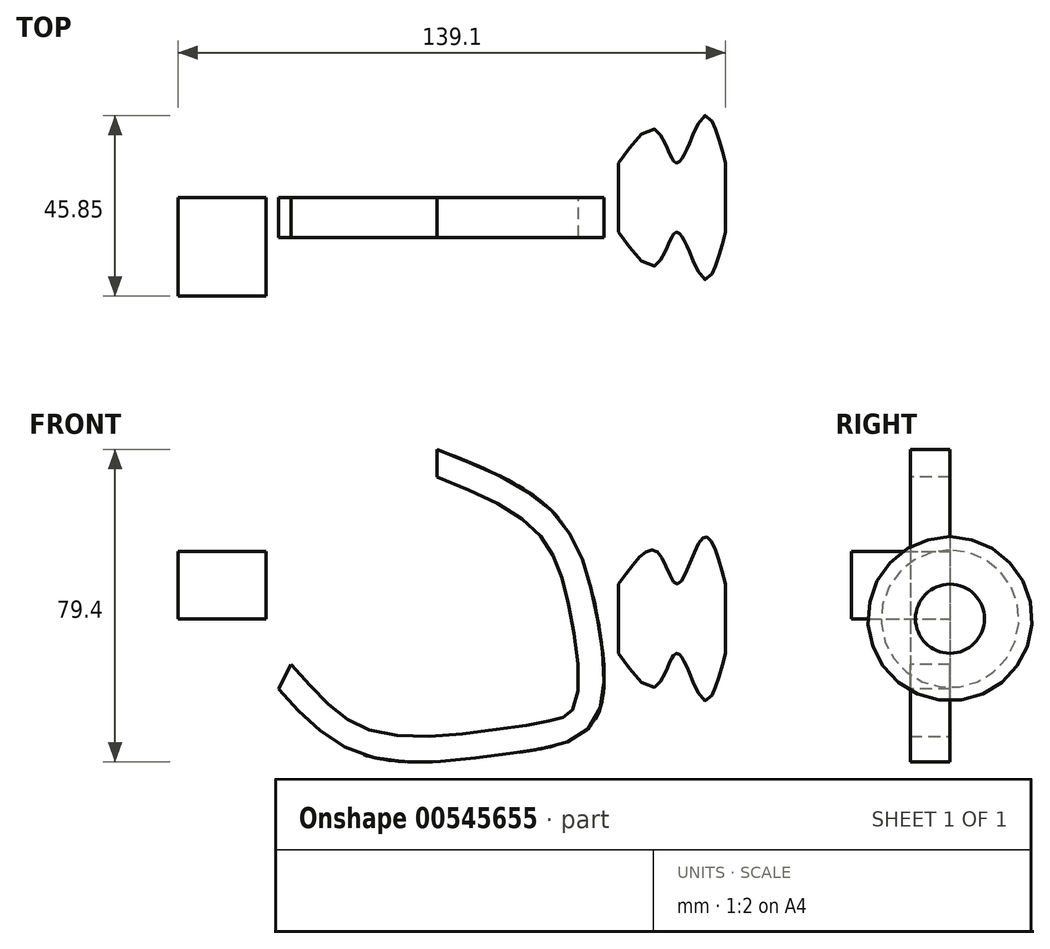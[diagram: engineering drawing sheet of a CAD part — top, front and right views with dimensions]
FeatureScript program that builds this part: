
annotation { "Feature Type Name" : "Feature", "Feature Type Description" : "" }
export const myFeature = defineFeature(function(context is Context, id is Id, definition is map)
    precondition{}
    {
        {
            var Q0;
            Q0=qCreatedBy(makeId("Front.planeOp"),FACE);
            var sketch = newSketch(context, id + "F0", { "sketchPlane" : qUnion([Q0])});
            skFitSpline(sketch, "E0", {"points": [v(0, 42.12) * mm, v(29.4, 25.89) * mm, v(39.93, 0) * mm, v(39.05, -25.89) * mm, v(18.87, -33.35) * mm, v(-18.43, -33.79) * mm, v(-39.93, -17.11) * mm], "startDerivative": vector(187.87, -73.92) * mm, "endDerivative": vector(-114.57, 127.43) * mm});
            skSolve(sketch);
        }
        {
            var Q0;
            Q0=qCreatedBy(makeId("Right.planeOp"),FACE);
            var sketch = newSketch(context, id + "F1", { "sketchPlane" : qUnion([Q0])});
            skLineSegment(sketch, "E1.bottom", {"start": v(0, 43) * mm, "end": v(-10.1, 43) * mm});
            skLineSegment(sketch, "E1.top", {"start": v(0, 35.98) * mm, "end": v(-10.1, 35.98) * mm});
            skLineSegment(sketch, "E1.left", {"start": v(0, 43) * mm, "end": v(0, 35.98) * mm});
            skLineSegment(sketch, "E1.right", {"start": v(-10.1, 43) * mm, "end": v(-10.1, 35.98) * mm});
            skSolve(sketch);
        }
        {
            var Q0;
            Q0=makeQuery(id+"F1.imprint","IMPRINT",FACE,{"disambiguationData":[TD([[makeQuery(id+"F1.imprint","IMPRINT",EDGE,{"derivedFrom":sQuery(id+"F1.wireOp",EDGE,"E1.bottom")}),1.0]])]});
            var Q1;
            Q1=sQuery(id+"F0.wireOp",EDGE,"E0");
            sweep(context, id + "F2", {"profiles" : qUnion([Q0]), "path" : qUnion([Q1])});
        }
        {
            var Q0;
            Q0=qCreatedBy(makeId("Front.planeOp"),FACE);
            var sketch = newSketch(context, id + "F3", { "sketchPlane" : qUnion([Q0])});
            skLineSegment(sketch, "E2.bottom", {"start": v(-65.82, 17.11) * mm, "end": v(-43.44, 17.11) * mm});
            skLineSegment(sketch, "E2.top", {"start": v(-65.82, 0) * mm, "end": v(-43.44, 0) * mm});
            skLineSegment(sketch, "E2.left", {"start": v(-65.82, 17.11) * mm, "end": v(-65.82, 0) * mm});
            skLineSegment(sketch, "E2.right", {"start": v(-43.44, 17.11) * mm, "end": v(-43.44, 0) * mm});
            skSolve(sketch);
        }
        {
            var Q0;
            Q0=makeQuery(id+"F3.imprint","IMPRINT",FACE,{"disambiguationData":[TD([[makeQuery(id+"F3.imprint","IMPRINT",EDGE,{"derivedFrom":sQuery(id+"F3.wireOp",EDGE,"E2.bottom")}),-1.0]])]});
            extrude(context, id + "F4", {"entities" : qUnion([Q0]), "depth" : 25 * mm, "offsetDistance" : 25 * mm});
        }
        {
            var Q0;
            Q0=qCreatedBy(makeId("Front.planeOp"),FACE);
            var sketch = newSketch(context, id + "F5", { "sketchPlane" : qUnion([Q0])});
            skLineSegment(sketch, "E3", {"start": v(46.07, 0) * mm, "end": v(46.07, 8.78) * mm});
            skFitSpline(sketch, "E4", {"points": [v(46.07, 8.78) * mm, v(55.73, 17.11) * mm, v(61, 8.78) * mm, v(67.58, 20.62) * mm, v(73.28, 8.78) * mm], "startDerivative": vector(42.12, 59.82) * mm, "endDerivative": vector(20.87, -77.63) * mm});
            skLineSegment(sketch, "E5", {"start": v(73.28, 8.78) * mm, "end": v(73.28, 0) * mm});
            skLineSegment(sketch, "E6", {"start": v(46.07, 0) * mm, "end": v(73.28, 0) * mm});
            skSolve(sketch);
        }
        {
            var Q0;
            Q0=makeQuery(id+"F5.imprint","IMPRINT",FACE,{"disambiguationData":[TD([[makeQuery(id+"F5.imprint","IMPRINT",EDGE,{"derivedFrom":sQuery(id+"F5.wireOp",EDGE,"E3")}),-1.0]])]});
            var Q1;
            Q1=sQuery(id+"F5.wireOp",EDGE,"E6");
            revolve(context, id + "F6", {"entities" : qUnion([Q0]), "axis" : qUnion([Q1]), "revolveType" : RevolveType.FULL});
        }
    });
